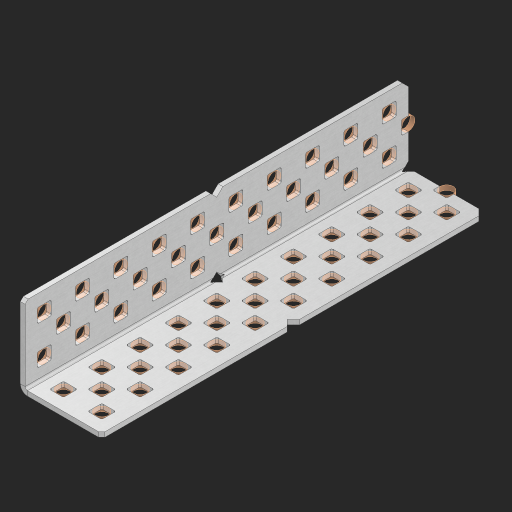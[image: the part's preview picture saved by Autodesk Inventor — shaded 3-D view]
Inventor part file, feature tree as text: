
AUTODESK INVENTOR PART (.ipt)
format: ipt  version: 2023 (Build 270158000, 158)  size: 1,006,592 bytes
history: native  units: in
note: dims shown in document units (in); Inventor stores cm internally (conversion verified against a paired STEP export)
features: other x66, extrude x58, sheet_metal_op x8, sketch x7, pattern_linear x2, mirror x1, chamfer x1
ambient origin geometry x8: Origin, YZ Plane, XZ Plane, XY Plane, X Axis, Y Axis, Z Axis, Center Point
bodies: Solid1 (feature_tree), Body (feature_tree)
feature tree (143):
  sheet_metal_op  "Flanges"
  sheet_metal_op  "Body Pattern"
  pattern_linear  "Center Pattern"  Spacing1=1.0in  [1 undecoded]
  other  "Arc Length"
  pattern_linear  "Notch Pattern"  Spacing1=0.25in  [1 undecoded]
  other  "Diagonal Plane"
  mirror  "Everything Mirrored"
  chamfer  "End Chamfer"
  sketch  "Sketch1"  dims[d0=1.0in]
  other  "Plate1"
  sketch  "Sketch2"  dims[d1=5.0in]
  other  "Plate2"
  sheet_metal_op  "Bend1"
  sheet_metal_op  "Corner1"
  sketch  "Sketch8"  dims[d2=0.0625in]
  sketch  "Sketch9"  dims[d3=0.0625in]
  other  "Srf91"
  sheet_metal_op  "Body Pattern Sketch"
  other  "Srf92"
  sketch  "Sketch13"  dims[d4=0.0312in]
  sketch  "Sketch15"  dims[d5=0.125in]
  sketch  "Sketch16"  dims[d6=0.0625in d7=1.0in d8=90.0deg d9=0.0312in d10=0.25in d11=0.0625in d12=0.0625in d49=0.182in d50=0.02in d52=0.25in d53=0.0625in d54=0.0in d55=0.172in d56=1.0in d57=0.0in d60=3.937in d62=0.5in d63=0.7874in d65=0.5in d85=0.1473in d86=0.1782in d89=0.0625in d90=0.0in d91=0.04in d92=0.0491in d95=2.5in d96=0.04in d97=0.25in d98=45.0deg d99=0.25in d106=0.182in d107=0.02in d108=0.5in d110=0.0625in d111=0.0in d112=0.172in d113=0.5in d114=0.0in d117=0.5in d123=0.25in d125=0.25in d126=0.0491in d127=0.1473in d128=0.08in d129=0.04in d130=2.5in]
  other  "Srf786"
  other  "Srf856"
  other  "Srf857"
  other  "Srf858"
  other  "Srf859"
  other  "Srf860"
  other  "Srf861"
  other  "Srf889"
  other  "Srf890"
  other  "Srf891"
  other  "Srf1275"
  other  "Srf1276"
  other  "Srf1278"
  other  "Srf1279"
  other  "Srf1280"
  other  "Srf1281"
  other  "Srf1282"
  other  "Srf1283"
  other  "Srf1277"
  other  "Srf1285"
  other  "Srf1286"
  other  "Srf1287"
  other  "Srf1383"
  other  "Srf1384"
  other  "Srf1385"
  other  "Srf1386"
  other  "Srf1387"
  other  "Srf1388"
  other  "Srf1389"
  other  "Srf1390"
  other  "Srf1391"
  other  "Srf1392"
  other  "Srf1393"
  other  "Srf1394"
  other  "Srf1445"
  other  "Srf1446"
  other  "Srf1447"
  other  "Srf1448"
  other  "Srf1449"
  other  "Srf1450"
  other  "Srf1475"
  other  "Srf1476"
  other  "Srf1477"
  other  "Srf1478"
  other  "Srf1479"
  other  "Srf1480"
  other  "Srf1481"
  other  "Srf1482"
  other  "Srf1483"
  other  "Srf1484"
  other  "Srf1485"
  other  "Srf1486"
  other  "Srf1537"
  other  "Srf1538"
  other  "Srf1539"
  other  "Srf1540"
  other  "Srf1541"
  other  "Srf1542"
  sheet_metal_op  "Body Stamp"
  sheet_metal_op  "Body Circle"
  other  "Center Stamp"
  other  "Center Circle"
  sheet_metal_op  "Notch"
  extrude  "ExtrusionSrf92"  Depth=0.0625in
  extrude  "ExtrusionSrf856"  Depth=0.0625in
  extrude  "ExtrusionSrf857"  Depth=2.5in
  extrude  "ExtrusionSrf858"  Depth=0.02in
  extrude  "ExtrusionSrf859"  Depth=2.5in
  extrude  "ExtrusionSrf860"  Depth=0.0625in
  extrude  "ExtrusionSrf861"  TaperAngle=0.0deg  [1 undecoded]
  extrude  "ExtrusionSrf889"  Depth=2.5in
  extrude  "ExtrusionSrf890"  Depth=1.0in TaperAngle=0.0deg
  extrude  "ExtrusionSrf891"  Depth=2.5in
  extrude  "ExtrusionSrf1275"  Depth=0.5in
  extrude  "ExtrusionSrf1276"  Depth=2.5in
  extrude  "ExtrusionSrf1277"  Depth=2.5in
  extrude  "ExtrusionSrf1278"  Depth=0.0625in
  extrude  "ExtrusionSrf1279"  Depth=2.5in TaperAngle=0.0deg
  extrude  "ExtrusionSrf1280"  Depth=2.5in
  extrude  "ExtrusionSrf1281"  Depth=2.5in TaperAngle=45.0deg
  extrude  "ExtrusionSrf1282"  Depth=2.5in
  extrude  "ExtrusionSrf1345"  Depth=2.5in
  extrude  "ExtrusionSrf1346"  Depth=0.02in
  extrude  "ExtrusionSrf1347"  Depth=0.5in
  extrude  "ExtrusionSrf1348"  Depth=0.0625in
  extrude  "ExtrusionSrf1383"  TaperAngle=0.0deg  [1 undecoded]
  extrude  "ExtrusionSrf1384"  Depth=2.5in
  extrude  "ExtrusionSrf1385"  Depth=0.5in TaperAngle=0.0deg
  extrude  "ExtrusionSrf1386"  Depth=0.5in
  extrude  "ExtrusionSrf1387"  Depth=2.5in
  extrude  "ExtrusionSrf1388"  Depth=2.5in
  extrude  "ExtrusionSrf1389"  Depth=2.5in
  extrude  "ExtrusionSrf1390"  Depth=2.5in
  extrude  "ExtrusionSrf1391"  Depth=2.5in
  extrude  "ExtrusionSrf1392"  Depth=2.5in
  extrude  "ExtrusionSrf1393"  Depth=2.5in
  extrude  "ExtrusionSrf1394"  [1 undecoded]
  extrude  "ExtrusionSrf1445"  [1 undecoded]
  extrude  "ExtrusionSrf1446"  [1 undecoded]
  extrude  "ExtrusionSrf1447"  [1 undecoded]
  extrude  "ExtrusionSrf1448"  [1 undecoded]
  extrude  "ExtrusionSrf1449"  [1 undecoded]
  extrude  "ExtrusionSrf1450"  [1 undecoded]
  extrude  "ExtrusionSrf1475"  [1 undecoded]
  extrude  "ExtrusionSrf1476"  [1 undecoded]
  extrude  "ExtrusionSrf1477"  [1 undecoded]
  extrude  "ExtrusionSrf1478"  [1 undecoded]
  extrude  "ExtrusionSrf1479"  [1 undecoded]
  extrude  "ExtrusionSrf1480"  [1 undecoded]
  extrude  "ExtrusionSrf1481"  [1 undecoded]
  extrude  "ExtrusionSrf1482"  [1 undecoded]
  extrude  "ExtrusionSrf1483"  [1 undecoded]
  extrude  "ExtrusionSrf1484"  [1 undecoded]
  extrude  "ExtrusionSrf1485"  [1 undecoded]
  extrude  "ExtrusionSrf1486"  [1 undecoded]
  extrude  "ExtrusionSrf1537"  [1 undecoded]
  extrude  "ExtrusionSrf1538"  [1 undecoded]
  extrude  "ExtrusionSrf1539"  [1 undecoded]
  extrude  "ExtrusionSrf1540"  [1 undecoded]
  extrude  "ExtrusionSrf1541"  [1 undecoded]
  extrude  "ExtrusionSrf1542"  [1 undecoded]
note: 29 required parameter values undecoded (feature->parameter linkage not recoverable at this tier; creation-order binding heuristic only, values carry confidence <= 0.55)
